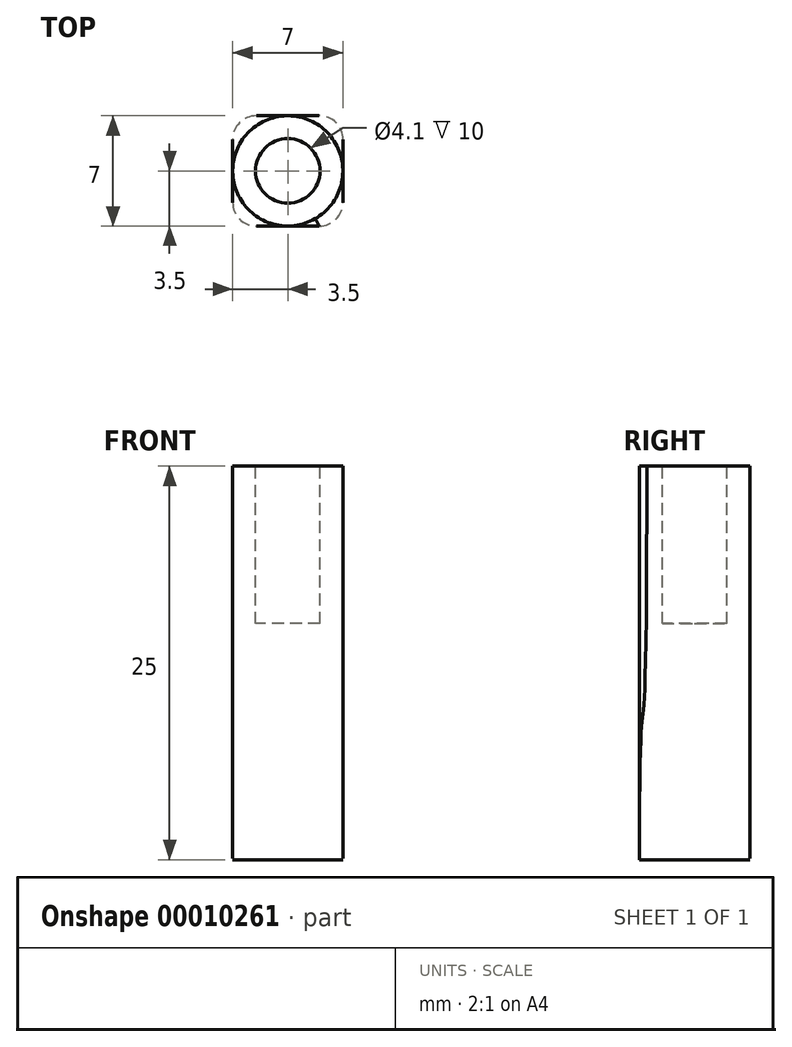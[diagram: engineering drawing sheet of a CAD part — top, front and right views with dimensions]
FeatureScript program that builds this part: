
annotation { "Feature Type Name" : "Feature", "Feature Type Description" : "" }
export const myFeature = defineFeature(function(context is Context, id is Id, definition is map)
    precondition{}
    {
        {
            var Q0;
            Q0=qCreatedBy(makeId("Top.planeOp"),FACE);
            var sketch = newSketch(context, id + "F0", { "sketchPlane" : qUnion([Q0])});
            skCircle(sketch, "E0", {"center": v(0, 0) * mm, "radius": 2.1 * mm, "construction": true});
            skLineSegment(sketch, "E1.rect.bottom", {"start": v(2, -3.5) * mm, "end": v(-2, -3.5) * mm});
            skLineSegment(sketch, "E1.rect.top", {"start": v(2, 3.5) * mm, "end": v(-2, 3.5) * mm});
            skLineSegment(sketch, "E1.rect.left", {"start": v(3.5, -2) * mm, "end": v(3.5, 2) * mm});
            skLineSegment(sketch, "E1.rect.right", {"start": v(-3.5, -2) * mm, "end": v(-3.5, 2) * mm});
            skPoint(sketch, "E2.visualSharp", {"position": v(-3.5, 3.5) * mm});
            skArc(sketch, "E2.filletArc", {"start": v(-2, 3.5) * mm, "mid": v(-3.06, 3.06) * mm, "end": v(-3.5, 2) * mm});
            skPoint(sketch, "E3.visualSharp", {"position": v(3.5, -3.5) * mm});
            skArc(sketch, "E3.filletArc", {"start": v(2, -3.5) * mm, "mid": v(3.06, -3.06) * mm, "end": v(3.5, -2) * mm});
            skPoint(sketch, "E4.visualSharp", {"position": v(3.5, 3.5) * mm});
            skArc(sketch, "E4.filletArc", {"start": v(3.5, 2) * mm, "mid": v(3.06, 3.06) * mm, "end": v(2, 3.5) * mm});
            skPoint(sketch, "E5.visualSharp", {"position": v(-3.5, -3.5) * mm});
            skArc(sketch, "E5.filletArc", {"start": v(-3.5, -2) * mm, "mid": v(-3.06, -3.06) * mm, "end": v(-2, -3.5) * mm});
            skSolve(sketch);
        }
        {
            var Q0;
            Q0=qCreatedBy(makeId("Top.planeOp"),FACE);
            cPlane(context, id + "F1", {"entities" : qUnion([Q0]), "cplaneType" : CPlaneType.OFFSET, "offset" : 25 * mm, "width" : 150 * mm, "height" : 150 * mm});
        }
        {
            var Q0;
            Q0=qCreatedBy(id+"F1.planeOp",FACE);
            var sketch = newSketch(context, id + "F2", { "sketchPlane" : qUnion([Q0])});
            skCircle(sketch, "E6", {"center": v(0, 0) * mm, "radius": 3.5 * mm});
            skCircle(sketch, "E7.1", {"center": v(0, 0) * mm, "radius": 2.1 * mm, "construction": true});
            skSolve(sketch);
        }
        {
            var Q0;
            Q0=makeQuery(id+"F2.imprint","IMPRINT",FACE,{"disambiguationData":[TD([[makeQuery(id+"F2.imprint","IMPRINT",EDGE,{"derivedFrom":sQuery(id+"F2.wireOp",EDGE,"E6")}),1.0]])]});
            var Q1;
            Q1=makeQuery(id+"F0.imprint","IMPRINT",FACE,{"disambiguationData":[TD([[makeQuery(id+"F0.imprint","IMPRINT",EDGE,{"derivedFrom":sQuery(id+"F0.wireOp",EDGE,"E1.rect.bottom")}),-1.0]])]});
            loft(context, id + "F3", {"startCondition" : LoftEndDerivativeType.NORMAL_TO_PROFILE, "startMagnitude" : 3, "endCondition" : LoftEndDerivativeType.NORMAL_TO_PROFILE, "endMagnitude" : 2, "sheetProfilesArray" : [{ "sheetProfileEntities" : qUnion([Q0]) }, { "sheetProfileEntities" : qUnion([Q1]) }]});
        }
        {
            var Q0;
            Q0=makeQuery(id+"F3.opLoft","CAP_FACE",FACE,{"disambiguationData":[OSD([makeQuery(id+"F2.imprint","IMPRINT",FACE,{"disambiguationData":[TD([[makeQuery(id+"F2.imprint","IMPRINT",EDGE,{"derivedFrom":sQuery(id+"F2.wireOp",EDGE,"E6")}),1.0]])]})])],"isStart":true});
            var sketch = newSketch(context, id + "F4", { "sketchPlane" : qUnion([Q0])});
            skCircle(sketch, "E8", {"center": v(0, 0) * mm, "radius": 2.05 * mm});
            skSolve(sketch);
        }
        {
            var Q0;
            Q0 = qSketchRegion(id + "F4", true);
            extrude(context, id + "F5", {"entities" : qUnion([Q0]), "operationType" : NewBodyOperationType.REMOVE, "oppositeDirection" : true, "depth" : 10 * mm});
        }
    });
